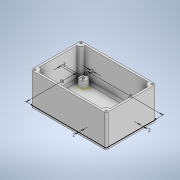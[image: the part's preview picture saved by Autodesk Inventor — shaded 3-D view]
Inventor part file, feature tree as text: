
AUTODESK INVENTOR PART (.ipt)
format: ipt  version: 2020.2 (Build 242310000, 310)  size: 240,128 bytes
history: native  units: mm
features: extrude x4, sketch x3, fillet x2
ambient origin geometry x8: Origin, YZ Plane, XZ Plane, XY Plane, X Axis, Y Axis, Z Axis, Center Point
bodies: Solid1 (feature_tree)
feature tree (9):
  extrude  "Extrusion1"  Depth=53.0mm
  sketch  "Sketch2"  dims[d2=2.0mm d3=7.5mm]
  extrude  "Extrusion7"  Depth=2.0mm
  extrude  "Extrusion8"  Depth=2.0mm
  extrude  "Extrusion9"  Depth=2.0mm
  fillet  "Fillet2"  Radius=2.0mm
  fillet  "Fillet3"  Radius=2.0mm
  sketch  "Sketch1"  dims[d0=33.0mm d1=53.0mm]
  sketch  "Sketch6"  dims[d4=7.5mm d5=0.0mm d6=75.0mm d10=50.0mm d11=2.0mm d24=2.0mm d129=4.0mm d132=2.0mm d133=2.0mm d134=2.0mm d135=2.0mm d136=0.0mm d137=30.0mm d138=0.0mm d139=10.0mm d140=0.0mm d141=2.0mm d142=2.0mm d28=0.5mm d29=0.872665mm d30=0.5mm d31=0.872665mm]
